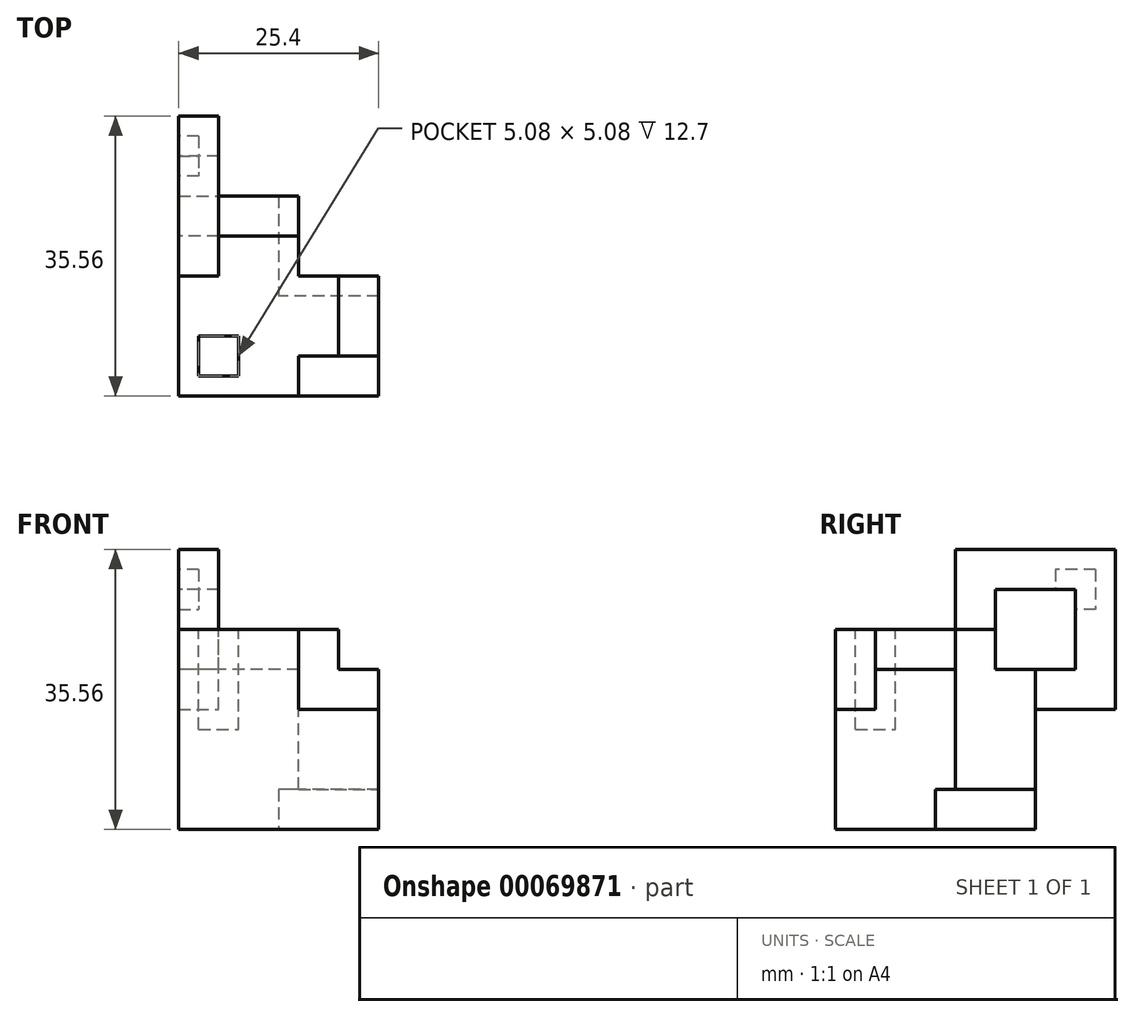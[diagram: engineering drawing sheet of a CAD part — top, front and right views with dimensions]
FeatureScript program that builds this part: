
annotation { "Feature Type Name" : "Feature", "Feature Type Description" : "" }
export const myFeature = defineFeature(function(context is Context, id is Id, definition is map)
    precondition{}
    {
        {
            var Q0;
            Q0=qCreatedBy(makeId("Top.planeOp"),FACE);
            var sketch = newSketch(context, id + "F0", { "sketchPlane" : qUnion([Q0])});
            skLineSegment(sketch, "E0.bottom", {"start": v(0, 0) * mm, "end": v(25.4, 0) * mm});
            skLineSegment(sketch, "E0.top", {"start": v(0, 25.4) * mm, "end": v(25.4, 25.4) * mm});
            skLineSegment(sketch, "E0.left", {"start": v(0, 0) * mm, "end": v(0, 25.4) * mm});
            skLineSegment(sketch, "E0.right", {"start": v(25.4, 0) * mm, "end": v(25.4, 25.4) * mm});
            skSolve(sketch);
        }
        {
            var Q0;
            Q0 = qSketchRegion(id + "F0", true);
            extrude(context, id + "F1", {"entities" : qUnion([Q0]), "depth" : 25.4 * mm});
        }
        {
            var Q0;
            Q0=makeQuery(id+"F1.opExtrude","SWEPT_FACE",FACE,{"disambiguationData":[OSD([sQuery(id+"F0.wireOp",EDGE,"E0.bottom")])]});
            var sketch = newSketch(context, id + "F2", { "sketchPlane" : qUnion([Q0])});
            skLineSegment(sketch, "E1.bottom", {"start": v(25.4, 25.4) * mm, "end": v(20.32, 25.4) * mm});
            skLineSegment(sketch, "E1.top", {"start": v(25.4, 20.32) * mm, "end": v(20.32, 20.32) * mm});
            skLineSegment(sketch, "E1.left", {"start": v(25.4, 25.4) * mm, "end": v(25.4, 20.32) * mm});
            skLineSegment(sketch, "E1.right", {"start": v(20.32, 25.4) * mm, "end": v(20.32, 20.32) * mm});
            skSolve(sketch);
        }
        {
            var Q0;
            Q0 = qSketchRegion(id + "F2", true);
            extrude(context, id + "F3", {"entities" : qUnion([Q0]), "operationType" : NewBodyOperationType.REMOVE, "oppositeDirection" : true, "depth" : 25.4 * mm});
        }
        {
            var Q0;
            Q0=makeQuery(id+"F1.opExtrude","SWEPT_FACE",FACE,{"disambiguationData":[OSD([sQuery(id+"F0.wireOp",EDGE,"E0.bottom")])]});
            var sketch = newSketch(context, id + "F4", { "sketchPlane" : qUnion([Q0])});
            skLineSegment(sketch, "E2.bottom", {"start": v(15.24, 15.24) * mm, "end": v(25.4, 15.24) * mm});
            skLineSegment(sketch, "E2.top", {"start": v(15.24, 25.4) * mm, "end": v(25.4, 25.4) * mm});
            skLineSegment(sketch, "E2.left", {"start": v(15.24, 15.24) * mm, "end": v(15.24, 25.4) * mm});
            skLineSegment(sketch, "E2.right", {"start": v(25.4, 15.24) * mm, "end": v(25.4, 25.4) * mm});
            skSolve(sketch);
        }
        {
            var Q0;
            Q0 = qSketchRegion(id + "F4", true);
            extrude(context, id + "F5", {"entities" : qUnion([Q0]), "operationType" : NewBodyOperationType.REMOVE, "oppositeDirection" : true, "depth" : 5.08 * mm});
        }
        {
            var Q0;
            Q0=makeQuery(id+"F1.opExtrude","SWEPT_FACE",FACE,{"disambiguationData":[OSD([sQuery(id+"F0.wireOp",EDGE,"E0.left")])]});
            var sketch = newSketch(context, id + "F6", { "sketchPlane" : qUnion([Q0])});
            skLineSegment(sketch, "E3.bottom", {"start": v(-15.24, 15.24) * mm, "end": v(-35.56, 15.24) * mm});
            skLineSegment(sketch, "E3.top", {"start": v(-15.24, 35.56) * mm, "end": v(-35.56, 35.56) * mm});
            skLineSegment(sketch, "E3.left", {"start": v(-15.24, 15.24) * mm, "end": v(-15.24, 35.56) * mm});
            skLineSegment(sketch, "E3.right", {"start": v(-35.56, 15.24) * mm, "end": v(-35.56, 35.56) * mm});
            skSolve(sketch);
        }
        {
            var Q0;
            Q0 = qSketchRegion(id + "F6", true);
            extrude(context, id + "F7", {"entities" : qUnion([Q0]), "operationType" : NewBodyOperationType.ADD, "oppositeDirection" : true, "depth" : 5.08 * mm});
        }
        {
            var Q0;
            Q0=makeQuery(id+"F7.boolean.opBoolean","MERGE",FACE,{"derivedFrom":[makeQuery(id+"F1.opExtrude","SWEPT_FACE",FACE,{"disambiguationData":[OSD([sQuery(id+"F0.wireOp",EDGE,"E0.left")])]}),makeQuery(id+"F7.opExtrude","CAP_FACE",FACE,{"disambiguationData":[OSD([sQuery(id+"F6.wireOp",EDGE,"E3.bottom"),sQuery(id+"F6.wireOp",EDGE,"E3.top"),sQuery(id+"F6.wireOp",EDGE,"E3.left"),sQuery(id+"F6.wireOp",EDGE,"E3.right")])],"isStart":true})]});
            var sketch = newSketch(context, id + "F8", { "sketchPlane" : qUnion([Q0])});
            skLineSegment(sketch, "E4.bottom", {"start": v(-20.32, 20.32) * mm, "end": v(-30.48, 20.32) * mm});
            skLineSegment(sketch, "E4.top", {"start": v(-20.32, 30.48) * mm, "end": v(-30.48, 30.48) * mm});
            skLineSegment(sketch, "E4.left", {"start": v(-20.32, 20.32) * mm, "end": v(-20.32, 30.48) * mm});
            skLineSegment(sketch, "E4.right", {"start": v(-30.48, 20.32) * mm, "end": v(-30.48, 30.48) * mm});
            skSolve(sketch);
        }
        {
            var Q0;
            Q0=makeQuery(id+"F8.imprint","IMPRINT",FACE,{"disambiguationData":[TD([[makeQuery(id+"F8.imprint","IMPRINT",EDGE,{"derivedFrom":sQuery(id+"F8.wireOp",EDGE,"E4.bottom")}),-1.0]])]});
            extrude(context, id + "F9", {"entities" : qUnion([Q0]), "operationType" : NewBodyOperationType.REMOVE, "oppositeDirection" : true, "depth" : 25.4 * mm});
        }
        {
            var Q0;
            Q0=makeQuery(id+"F1.opExtrude","CAP_FACE",FACE,{"disambiguationData":[OSD([sQuery(id+"F0.wireOp",EDGE,"E0.bottom"),sQuery(id+"F0.wireOp",EDGE,"E0.top"),sQuery(id+"F0.wireOp",EDGE,"E0.left"),sQuery(id+"F0.wireOp",EDGE,"E0.right")])],"isStart":false});
            var sketch = newSketch(context, id + "F10", { "sketchPlane" : qUnion([Q0])});
            skLineSegment(sketch, "E5.bottom", {"start": v(2.54, 2.54) * mm, "end": v(7.62, 2.54) * mm});
            skLineSegment(sketch, "E5.top", {"start": v(2.54, 7.62) * mm, "end": v(7.62, 7.62) * mm});
            skLineSegment(sketch, "E5.left", {"start": v(2.54, 2.54) * mm, "end": v(2.54, 7.62) * mm});
            skLineSegment(sketch, "E5.right", {"start": v(7.62, 2.54) * mm, "end": v(7.62, 7.62) * mm});
            skSolve(sketch);
        }
        {
            var Q0;
            Q0 = qSketchRegion(id + "F10", true);
            extrude(context, id + "F11", {"entities" : qUnion([Q0]), "operationType" : NewBodyOperationType.REMOVE, "oppositeDirection" : true, "depth" : 12.7 * mm});
        }
        {
            var Q0;
            Q0=makeQuery(id+"F1.opExtrude","CAP_FACE",FACE,{"disambiguationData":[OSD([sQuery(id+"F0.wireOp",EDGE,"E0.bottom"),sQuery(id+"F0.wireOp",EDGE,"E0.top"),sQuery(id+"F0.wireOp",EDGE,"E0.left"),sQuery(id+"F0.wireOp",EDGE,"E0.right")])],"isStart":false});
            var sketch = newSketch(context, id + "F12", { "sketchPlane" : qUnion([Q0])});
            skLineSegment(sketch, "E6.bottom", {"start": v(15.24, 15.24) * mm, "end": v(25.4, 15.24) * mm});
            skLineSegment(sketch, "E6.top", {"start": v(15.24, 25.4) * mm, "end": v(25.4, 25.4) * mm});
            skLineSegment(sketch, "E6.left", {"start": v(15.24, 15.24) * mm, "end": v(15.24, 25.4) * mm});
            skLineSegment(sketch, "E6.right", {"start": v(25.4, 15.24) * mm, "end": v(25.4, 25.4) * mm});
            skSolve(sketch);
        }
        {
            var Q0;
            Q0 = qSketchRegion(id + "F12", true);
            extrude(context, id + "F13", {"entities" : qUnion([Q0]), "operationType" : NewBodyOperationType.REMOVE, "oppositeDirection" : true, "depth" : 25.4 * mm});
        }
        {
            var Q0;
            Q0=makeQuery(id+"F1.opExtrude","CAP_FACE",FACE,{"disambiguationData":[OSD([sQuery(id+"F0.wireOp",EDGE,"E0.bottom"),sQuery(id+"F0.wireOp",EDGE,"E0.top"),sQuery(id+"F0.wireOp",EDGE,"E0.left"),sQuery(id+"F0.wireOp",EDGE,"E0.right")])],"isStart":true});
            var sketch = newSketch(context, id + "F14", { "sketchPlane" : qUnion([Q0])});
            skLineSegment(sketch, "E7.bottom", {"start": v(25.4, -25.4) * mm, "end": v(12.7, -25.4) * mm});
            skLineSegment(sketch, "E7.top", {"start": v(25.4, -12.7) * mm, "end": v(12.7, -12.7) * mm});
            skLineSegment(sketch, "E7.left", {"start": v(25.4, -25.4) * mm, "end": v(25.4, -12.7) * mm});
            skLineSegment(sketch, "E7.right", {"start": v(12.7, -25.4) * mm, "end": v(12.7, -12.7) * mm});
            skSolve(sketch);
        }
        {
            var Q0;
            Q0 = qSketchRegion(id + "F14", true);
            extrude(context, id + "F15", {"entities" : qUnion([Q0]), "operationType" : NewBodyOperationType.REMOVE, "oppositeDirection" : true, "depth" : 5.08 * mm});
        }
        {
            var Q0;
            Q0=makeQuery(id+"F7.boolean.opBoolean","MERGE",FACE,{"derivedFrom":[makeQuery(id+"F1.opExtrude","SWEPT_FACE",FACE,{"disambiguationData":[OSD([sQuery(id+"F0.wireOp",EDGE,"E0.left")])]}),makeQuery(id+"F7.opExtrude","CAP_FACE",FACE,{"disambiguationData":[OSD([sQuery(id+"F6.wireOp",EDGE,"E3.bottom"),sQuery(id+"F6.wireOp",EDGE,"E3.top"),sQuery(id+"F6.wireOp",EDGE,"E3.left"),sQuery(id+"F6.wireOp",EDGE,"E3.right")])],"isStart":true})]});
            var sketch = newSketch(context, id + "F16", { "sketchPlane" : qUnion([Q0])});
            skLineSegment(sketch, "E8.bottom", {"start": v(-33.02, 33.02) * mm, "end": v(-27.94, 33.02) * mm});
            skLineSegment(sketch, "E8.top", {"start": v(-33.02, 27.94) * mm, "end": v(-27.94, 27.94) * mm});
            skLineSegment(sketch, "E8.left", {"start": v(-33.02, 33.02) * mm, "end": v(-33.02, 27.94) * mm});
            skLineSegment(sketch, "E8.right", {"start": v(-27.94, 33.02) * mm, "end": v(-27.94, 27.94) * mm});
            skSolve(sketch);
        }
        {
            var Q0;
            Q0 = qSketchRegion(id + "F16", true);
            extrude(context, id + "F17", {"entities" : qUnion([Q0]), "operationType" : NewBodyOperationType.REMOVE, "oppositeDirection" : true, "depth" : 2.54 * mm});
        }
    });
